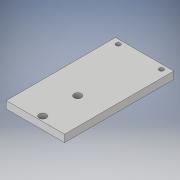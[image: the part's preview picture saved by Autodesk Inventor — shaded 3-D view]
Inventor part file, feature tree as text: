
AUTODESK INVENTOR PART (.ipt)
format: ipt  version: 2019.4 (Build 234330000, 330)  size: 112,640 bytes
history: native  units: in
note: dims shown in document units (in); Inventor stores cm internally (conversion verified against a paired STEP export)
features: sketch x3, hole x2, extrude x1
ambient origin geometry x8: Origin, YZ Plane, XZ Plane, XY Plane, X Axis, Y Axis, Z Axis, Center Point
bodies: Solid1 (feature_tree)
feature tree (6):
  extrude  "Extrusion1"  Depth=5.9055in
  hole  "Hole1"  [1 undecoded]
  hole  "Hole2"  [1 undecoded]
  sketch  "Sketch1"  dims[d0=3.1496in d1=5.9055in]
  sketch  "Sketch2"  dims[d2=0.3937in d3=0.0in]
  sketch  "Sketch3"  dims[d4=0.2362in d5=0.75in d6=0.119in d7=0.25in d8=0.5635in d9=0.3937in d10=0.8108in d11=0.3937in d12=0.75in d13=0.119in d14=0.25in d15=0.5635in d16=0.3937in d17=0.8108in d18=0.75in d19=0.8108in d20=0.0625in d21=0.75in d22=0.375in]
note: 2 required parameter values undecoded (feature->parameter linkage not recoverable at this tier; creation-order binding heuristic only, values carry confidence <= 0.55)
